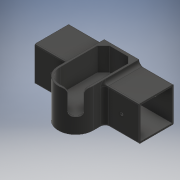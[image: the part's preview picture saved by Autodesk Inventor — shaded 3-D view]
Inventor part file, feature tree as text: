
AUTODESK INVENTOR PART (.ipt)
format: ipt  version: 2019.4 (Build 234330000, 330)  size: 317,952 bytes
history: native  units: mm
features: extrude x9, sketch x6, fillet x5, chamfer x1
ambient origin geometry x8: Origin, YZ Plane, XZ Plane, XY Plane, X Axis, Y Axis, Z Axis, Center Point
bodies: Solid1 (feature_tree)
feature tree (21):
  sketch  "Sketch1"  dims[d0=40.0mm d1=74.8mm]
  extrude  "Extrusion1"  Depth=40.0mm
  extrude  "Extrusion2"  Depth=45.0mm
  extrude  "Extrusion4"  Depth=17.5mm
  sketch  "Sketch2"  dims[d2=79.8mm d3=45.0mm]
  fillet  "Fillet1"  Radius=20.4mm
  fillet  "Fillet2"  Radius=20.0mm
  extrude  "Extrusion5"  Depth=20.0mm TaperAngle=0.0deg
  extrude  "Extrusion6"  Depth=2.5mm
  fillet  "Fillet5"  Radius=2.5mm
  fillet  "Fillet6"  Radius=50.0mm
  extrude  "Extrusion7"  Depth=8.0mm
  sketch  "Sketch8"  dims[d19=10.0mm d20=8.75mm d28=20.0mm d29=22.5mm d42=45.0mm d43=45.0mm d44=41.0mm d45=41.0mm d46=45.0mm d47=0.0mm d53=45.0mm d54=45.0mm d55=41.0mm d56=41.0mm d57=2.0mm d58=2.0mm d59=45.0mm d60=0.0mm d61=1.5mm d62=5.0mm d63=45.0mm d64=45.0mm d65=45.0mm d66=45.0mm d74=4.0mm d75=4.0mm d76=45.0mm d77=0.0mm d78=22.5mm d79=15.0mm d80=22.5mm d81=22.5mm d82=22.5mm d83=15.0mm d84=31.819805mm d85=30.0mm d86=0.0mm d87=5.0mm d88=42.0mm d89=40.0mm d90=9.0mm d91=30.0mm d92=0.0mm d93=8.0mm d94=2.0mm d95=45.0deg d96=4.0mm d97=90.0deg d98=8.0mm d99=75.0mm d100=0.0mm]
  extrude  "Extrusion8"  Depth=20.0mm
  fillet  "Fillet7"  Radius=22.5mm
  extrude  "Extrusion9"  Depth=45.0mm
  chamfer  "Chamfer2"  Distance=45.0mm
  extrude  "Extrusion10"  Depth=41.0mm
  sketch  "Sketch4"  dims[d4=17.5mm d5=17.5mm d6=20.4mm d7=20.0mm]
  sketch  "Sketch6"  dims[d8=20.0mm d9=0.0mm d10=50.0mm d11=0.0mm]
  sketch  "Sketch7"  dims[d12=40.0mm d13=2.5mm d14=2.5mm d17=50.0mm d18=0.0mm]
